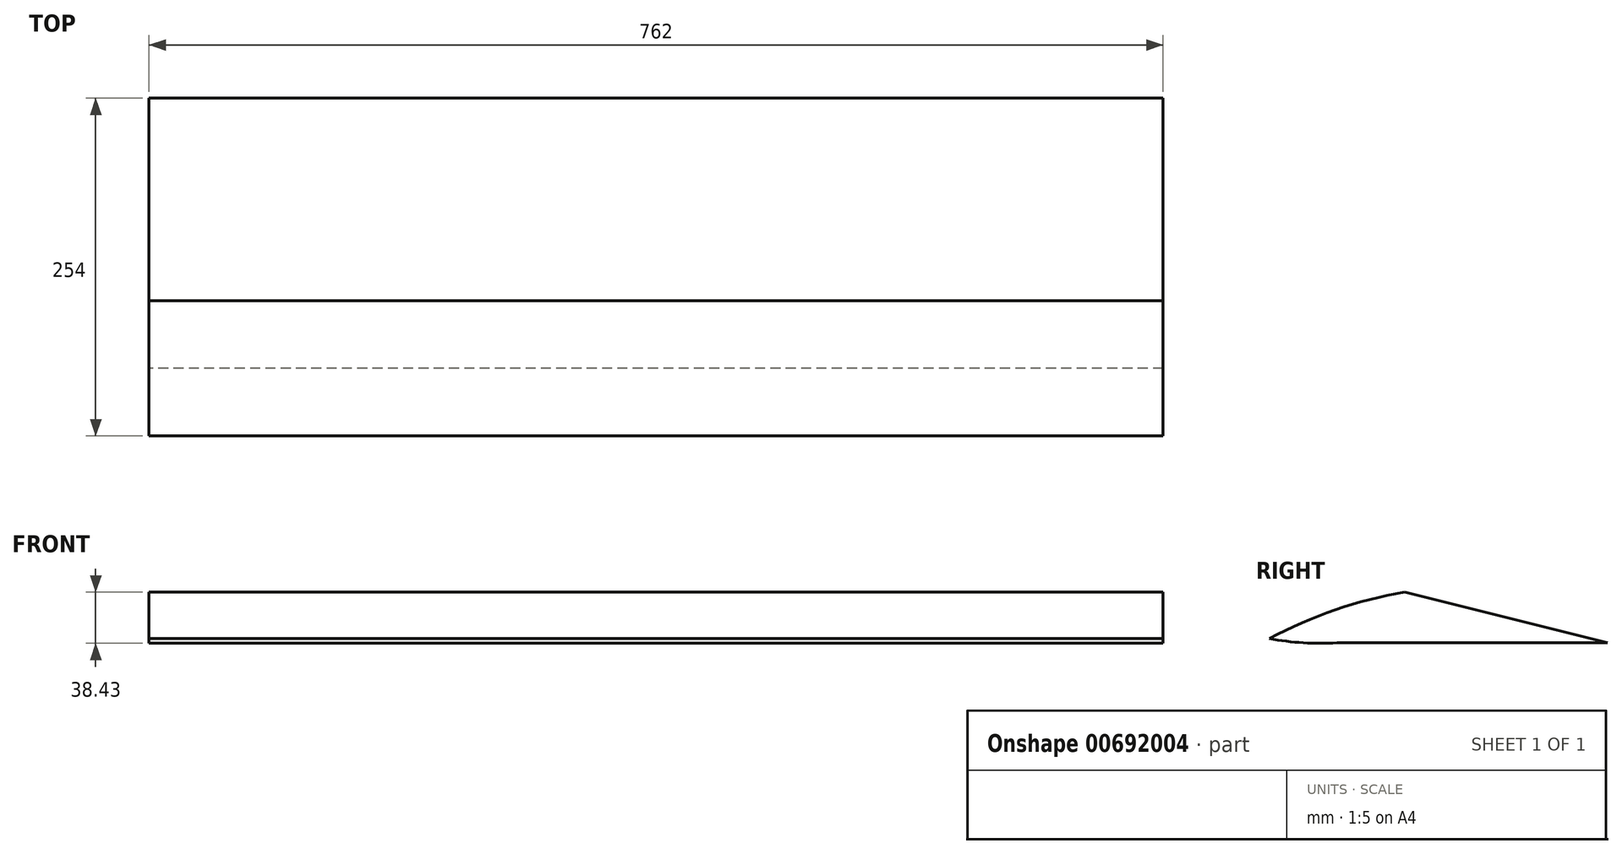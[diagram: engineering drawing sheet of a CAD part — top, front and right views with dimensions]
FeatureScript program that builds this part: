
annotation { "Feature Type Name" : "Feature", "Feature Type Description" : "" }
export const myFeature = defineFeature(function(context is Context, id is Id, definition is map)
    precondition{}
    {
        {
            var Q0;
            Q0=qCreatedBy(makeId("Right.planeOp"),FACE);
            var sketch = newSketch(context, id + "F0", { "sketchPlane" : qUnion([Q0])});
            skLineSegment(sketch, "E0.bottom", {"start": v(-127, 19.05) * mm, "end": v(127, 19.05) * mm});
            skLineSegment(sketch, "E0.top", {"start": v(-127, -19.05) * mm, "end": v(-120.65, -19.05) * mm});
            skLineSegment(sketch, "E0.left", {"start": v(-127, 19.05) * mm, "end": v(-127, -19.05) * mm});
            skLineSegment(sketch, "E0.right", {"start": v(127, 19.05) * mm, "end": v(127, -19.05) * mm});
            skPoint(sketch, "E0.middle", {"position": v(0, 0) * mm});
            skLineSegment(sketch, "E1", {"start": v(-127, -19.05) * mm, "end": v(-127, -15.88) * mm});
            skLineSegment(sketch, "E2", {"start": v(-127, 19.05) * mm, "end": v(-76.2, 19.05) * mm});
            skLineSegment(sketch, "E3", {"start": v(-76.2, 19.05) * mm, "end": v(-76.2, 6.35) * mm});
            skLineSegment(sketch, "E4", {"start": v(-127, 19.05) * mm, "end": v(-25.4, 19.05) * mm});
            skLineSegment(sketch, "E5", {"start": v(-25.4, 19.05) * mm, "end": v(127, -19.05) * mm});
            skArc(sketch, "E6", {"start": v(-25.4, 19.05) * mm, "mid": v(-77.67, 5.85) * mm, "end": v(-127, -15.88) * mm});
            skLineSegment(sketch, "E7", {"start": v(-76.2, 6.35) * mm, "end": v(-76.2, -19.05) * mm});
            skPoint(sketch, "E7.endSnap0", {"position": v(-123.83, -19.05) * mm});
            skPoint(sketch, "E8.start.orphan", {"position": v(-123.83, -17.46) * mm});
            skLineSegment(sketch, "E9", {"start": v(-123.83, -17.46) * mm, "end": v(-123.83, -19.05) * mm});
            skLineSegment(sketch, "E10", {"start": v(-100.01, -17.46) * mm, "end": v(-76.2, -17.46) * mm});
            skArc(sketch, "E11", {"start": v(-127, -15.88) * mm, "mid": v(-101.7, -18.95) * mm, "end": v(-76.2, -19.05) * mm});
            skLineSegment(sketch, "E12.trimOffspring", {"start": v(-76.2, -19.05) * mm, "end": v(127, -19.05) * mm});
            skSolve(sketch);
        }
        {
            var Q0;
            {var subQ0=sQuery(id+"F0.wireOp",EDGE,"NXUMzUXI-zmKo-8R2R-3vWu-fJcBiUhiakpH");Q0=makeQuery(id+"F0.imprint","IMPRINT",FACE,{"disambiguationData":[TD([[makeQuery(id+"F0.imprint","IMPRINT",EDGE,{"derivedFrom":subQ0}),-1.0]])]});}
            var Q1;
            {var subQ3=sQuery(id+"F0.wireOp",EDGE,"E11");Q1=makeQuery(id+"F0.imprint","IMPRINT",FACE,{"disambiguationData":[TD([[makeQuery(id+"F0.imprint","IMPRINT",EDGE,{"derivedFrom":subQ3}),1.0]])]});}
            var Q2;
            {var subQ5=sQuery(id+"F0.wireOp",EDGE,"E5");Q2=makeQuery(id+"F0.imprint","IMPRINT",FACE,{"disambiguationData":[TD([[makeQuery(id+"F0.imprint","IMPRINT",EDGE,{"derivedFrom":subQ5}),-1.0]])]});}
            extrude(context, id + "F1", {"entities" : qUnion([Q0, Q1, Q2]), "depth" : 762 * mm, "offsetDistance" : 25.4 * mm});
        }
    });
